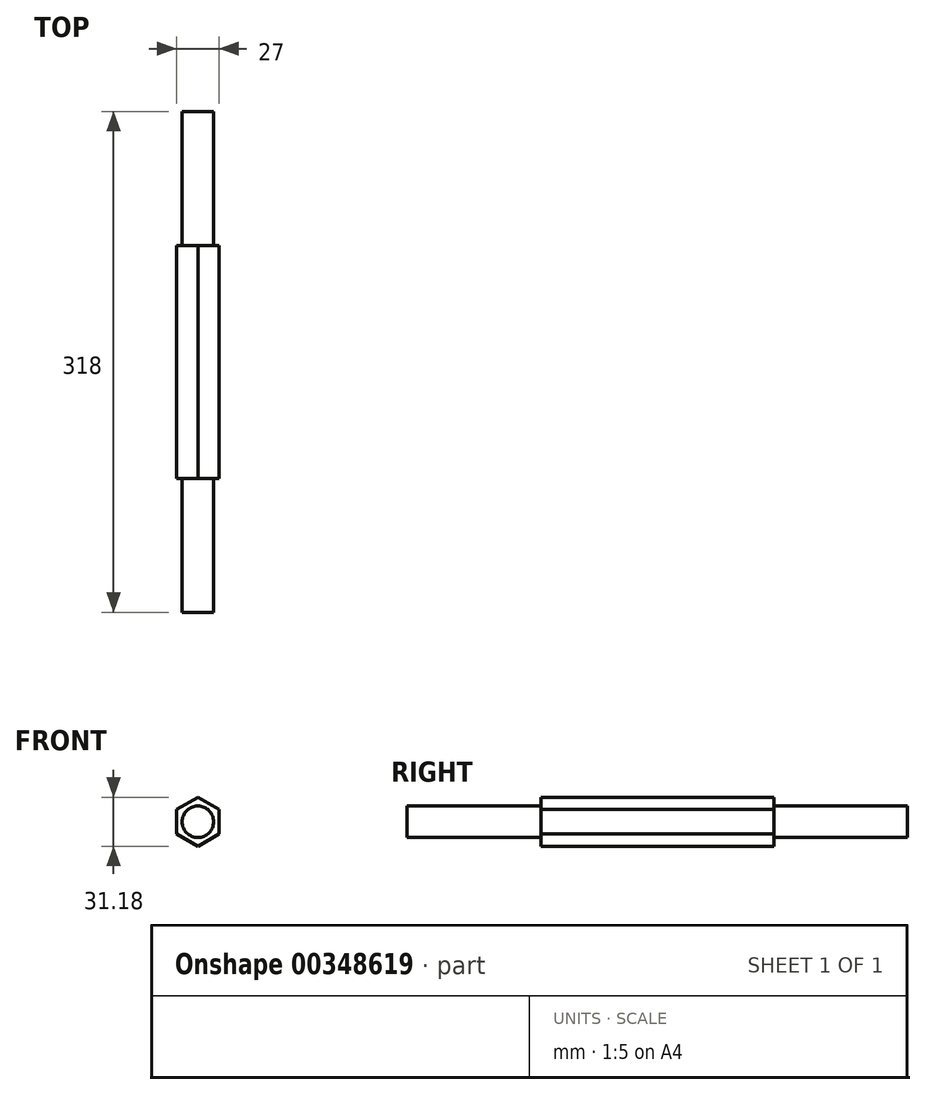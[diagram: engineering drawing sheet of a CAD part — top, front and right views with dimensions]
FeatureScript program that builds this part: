
annotation { "Feature Type Name" : "Feature", "Feature Type Description" : "" }
export const myFeature = defineFeature(function(context is Context, id is Id, definition is map)
    precondition{}
    {
        {
            var Q0;
            Q0=qCreatedBy(makeId("Front.planeOp"),FACE);
            var sketch = newSketch(context, id + "F0", { "sketchPlane" : qUnion([Q0])});
            skCircle(sketch, "E0.cCircle", {"center": v(0, 0) * mm, "radius": 13.5 * mm, "construction": true});
            skLineSegment(sketch, "E0.0", {"start": v(13.5, 7.8) * mm, "end": v(13.5, -7.8) * mm});
            skLineSegment(sketch, "E0.1", {"start": v(13.5, -7.8) * mm, "end": v(0, -15.59) * mm});
            skLineSegment(sketch, "E0.2", {"start": v(0, -15.59) * mm, "end": v(-13.5, -7.8) * mm});
            skLineSegment(sketch, "E0.3", {"start": v(-13.5, -7.8) * mm, "end": v(-13.5, 7.8) * mm});
            skLineSegment(sketch, "E0.4", {"start": v(-13.5, 7.8) * mm, "end": v(0, 15.59) * mm});
            skLineSegment(sketch, "E0.5", {"start": v(0, 15.59) * mm, "end": v(13.5, 7.8) * mm});
            skPoint(sketch, "E0.0.midPoint", {"position": v(13.5, 0) * mm});
            skSolve(sketch);
        }
        {
            var Q0;
            Q0=makeQuery(id+"F0.imprint","IMPRINT",FACE,{"disambiguationData":[TD([[makeQuery(id+"F0.imprint","IMPRINT",EDGE,{"derivedFrom":sQuery(id+"F0.wireOp",EDGE,"E0.0")}),-1.0]])]});
            extrude(context, id + "F1", {"entities" : qUnion([Q0]), "depth" : 74 * mm});
        }
        {
            var Q0;
            Q0=makeQuery(id+"F1.opExtrude","CAP_FACE",FACE,{"disambiguationData":[OSD([sQuery(id+"F0.wireOp",EDGE,"E0.0"),sQuery(id+"F0.wireOp",EDGE,"E0.1"),sQuery(id+"F0.wireOp",EDGE,"E0.2"),sQuery(id+"F0.wireOp",EDGE,"E0.3"),sQuery(id+"F0.wireOp",EDGE,"E0.4"),sQuery(id+"F0.wireOp",EDGE,"E0.5")])],"isStart":false});
            var sketch = newSketch(context, id + "F2", { "sketchPlane" : qUnion([Q0])});
            skCircle(sketch, "E1", {"center": v(0, 0) * mm, "radius": 10 * mm});
            skSolve(sketch);
        }
        {
            var Q0;
            Q0=makeQuery(id+"F2.imprint","IMPRINT",FACE,{"disambiguationData":[TD([[makeQuery(id+"F2.imprint","IMPRINT",EDGE,{"derivedFrom":sQuery(id+"F2.wireOp",EDGE,"E1")}),1.0]])]});
            extrude(context, id + "F3", {"entities" : qUnion([Q0]), "operationType" : NewBodyOperationType.ADD, "depth" : (159 - 74) * mm});
        }
        {
            var Q0;
            Q0=makeQuery(id+"F1.opExtrude","SWEPT_BODY",BODY,{"disambiguationData":[OSD([sQuery(id+"F0.wireOp",EDGE,"E0.0"),sQuery(id+"F0.wireOp",EDGE,"E0.1"),sQuery(id+"F0.wireOp",EDGE,"E0.2"),sQuery(id+"F0.wireOp",EDGE,"E0.3"),sQuery(id+"F0.wireOp",EDGE,"E0.4"),sQuery(id+"F0.wireOp",EDGE,"E0.5")])]});
            var Q1;
            Q1=makeQuery(id+"F1.opExtrude","CAP_FACE",FACE,{"disambiguationData":[OSD([sQuery(id+"F0.wireOp",EDGE,"E0.0"),sQuery(id+"F0.wireOp",EDGE,"E0.1"),sQuery(id+"F0.wireOp",EDGE,"E0.2"),sQuery(id+"F0.wireOp",EDGE,"E0.3"),sQuery(id+"F0.wireOp",EDGE,"E0.4"),sQuery(id+"F0.wireOp",EDGE,"E0.5")])],"isStart":true});
            mirror(context, id + "F4", {"operationType" : NewBodyOperationType.ADD, "entities" : qUnion([Q0]), "mirrorPlane" : qUnion([Q1])});
        }
    });
